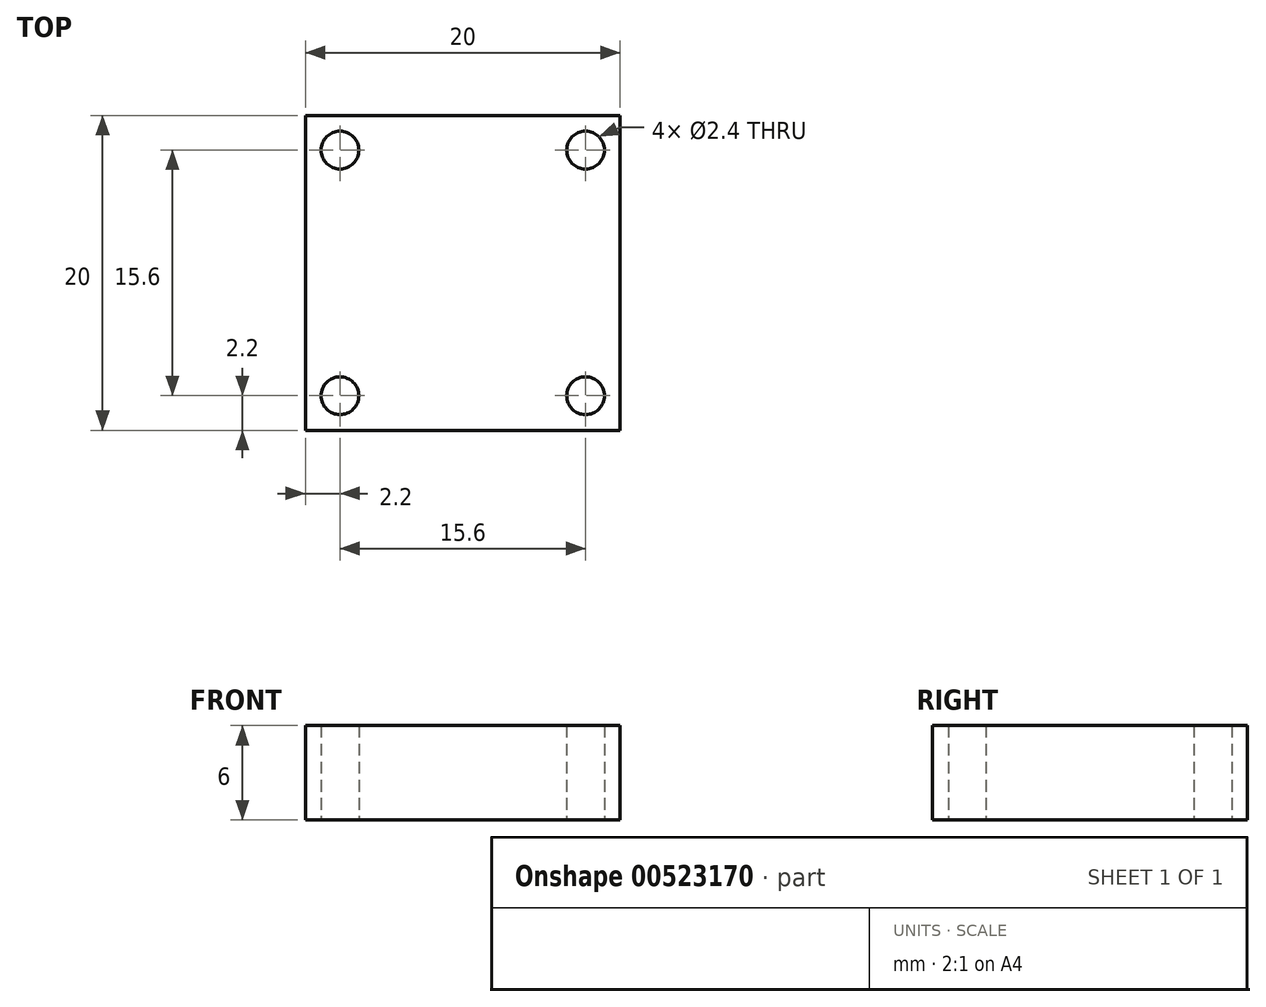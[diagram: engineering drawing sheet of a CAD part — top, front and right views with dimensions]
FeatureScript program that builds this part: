
annotation { "Feature Type Name" : "Feature", "Feature Type Description" : "" }
export const myFeature = defineFeature(function(context is Context, id is Id, definition is map)
    precondition{}
    {
        {
            var Q0;
            Q0=qCreatedBy(makeId("Top.planeOp"),FACE);
            var sketch = newSketch(context, id + "F0", { "sketchPlane" : qUnion([Q0])});
            skLineSegment(sketch, "E0.bottom", {"start": v(-10, 10) * mm, "end": v(10, 10) * mm});
            skLineSegment(sketch, "E0.top", {"start": v(-10, -10) * mm, "end": v(10, -10) * mm});
            skLineSegment(sketch, "E0.left", {"start": v(-10, 10) * mm, "end": v(-10, -10) * mm});
            skLineSegment(sketch, "E0.right", {"start": v(10, 10) * mm, "end": v(10, -10) * mm});
            skCircle(sketch, "E1", {"center": v(-7.8, 7.8) * mm, "radius": 1.2 * mm});
            skCircle(sketch, "E2", {"center": v(7.8, 7.8) * mm, "radius": 1.2 * mm});
            skCircle(sketch, "E3", {"center": v(7.8, -7.8) * mm, "radius": 1.2 * mm});
            skCircle(sketch, "E4", {"center": v(-7.8, -7.8) * mm, "radius": 1.2 * mm});
            skSolve(sketch);
        }
        {
            var Q0;
            Q0=makeQuery(id+"F0.imprint","IMPRINT",FACE,{"disambiguationData":[TD([[makeQuery(id+"F0.imprint","IMPRINT",EDGE,{"derivedFrom":sQuery(id+"F0.wireOp",EDGE,"E0.bottom")}),-1.0]])]});
            extrude(context, id + "F1", {"entities" : qUnion([Q0]), "depth" : 6 * mm, "offsetDistance" : 25 * mm});
        }
    });
